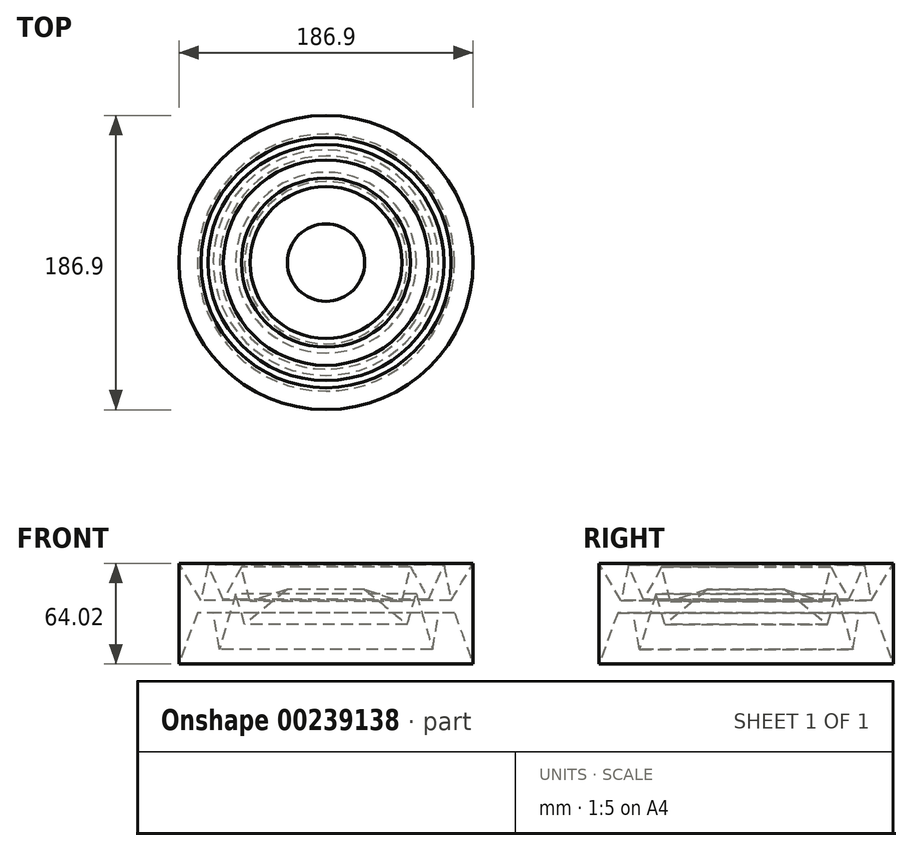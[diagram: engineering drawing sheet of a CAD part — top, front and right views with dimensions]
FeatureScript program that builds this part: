
annotation { "Feature Type Name" : "Feature", "Feature Type Description" : "" }
export const myFeature = defineFeature(function(context is Context, id is Id, definition is map)
    precondition{}
    {
        {
            var Q0;
            Q0=qCreatedBy(makeId("Front.planeOp"),FACE);
            var sketch = newSketch(context, id + "F0", { "sketchPlane" : qUnion([Q0])});
            skLineSegment(sketch, "E0", {"start": v(48.24, 23.21) * mm, "end": v(53.7, 45.05) * mm});
            skLineSegment(sketch, "E1", {"start": v(53.7, 45.05) * mm, "end": v(65.23, 24.42) * mm});
            skLineSegment(sketch, "E2", {"start": v(65.23, 24.42) * mm, "end": v(74.94, 46.27) * mm});
            skLineSegment(sketch, "E3", {"start": v(74.94, 46.27) * mm, "end": v(79.5, 23.82) * mm});
            skLineSegment(sketch, "E4", {"start": v(79.5, 23.82) * mm, "end": v(93.45, 47.48) * mm});
            skLineSegment(sketch, "E5", {"start": v(93.45, 47.48) * mm, "end": v(93.45, -16.54) * mm});
            skLineSegment(sketch, "E6", {"start": v(93.45, -16.54) * mm, "end": v(81.61, 15.93) * mm});
            skLineSegment(sketch, "E7", {"start": v(81.61, 15.93) * mm, "end": v(71.6, 15.93) * mm});
            skLineSegment(sketch, "E8", {"start": v(71.6, 15.93) * mm, "end": v(67.66, -7.13) * mm});
            skLineSegment(sketch, "E9", {"start": v(67.66, -7.13) * mm, "end": v(57.34, 28.06) * mm});
            skLineSegment(sketch, "E10", {"start": v(57.34, 28.06) * mm, "end": v(51.58, 8.65) * mm});
            skLineSegment(sketch, "E11", {"start": v(51.58, 8.65) * mm, "end": v(24.58, 30.8) * mm});
            skLineSegment(sketch, "E12", {"start": v(24.58, 30.8) * mm, "end": v(48.24, 23.21) * mm});
            skLineSegment(sketch, "E13", {"start": v(0, 42.02) * mm, "end": v(0, -36.56) * mm, "construction": true});
            skSolve(sketch);
        }
        {
            var Q0;
            Q0 = qSketchRegion(id + "F0", true);
            var Q1;
            Q1=sQuery(id+"F0.wireOp",EDGE,"E13");
            revolve(context, id + "F1", {"entities" : qUnion([Q0]), "axis" : qUnion([Q1]), "revolveType" : RevolveType.FULL});
        }
    });
